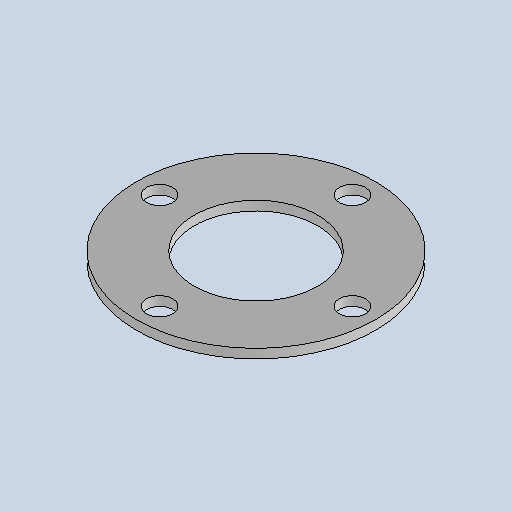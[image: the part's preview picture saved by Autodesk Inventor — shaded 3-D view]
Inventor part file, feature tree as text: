
AUTODESK INVENTOR PART (.ipt)
format: ipt  version: 2025.1 (Build 291241020, 241B)  size: 143,872 bytes
history: native  units: mm
features: other x3, sketch x2, sheet_metal_op x1, pattern_circular x1
ambient origin geometry x8: Origin, YZ Plane, XZ Plane, XY Plane, X Axis, Y Axis, Z Axis, Center Point
bodies: Solid1 (feature_tree)
feature tree (7):
  sheet_metal_op  "Face1"
  pattern_circular  "Circular Pattern1"  Count=8  [1 undecoded]
  sketch  "Sketch1"  dims[d2=6.0mm]
  other  "Plate1"
  sketch  "Sketch5"  dims[d22=155.0mm d23=80.0mm d24=62.5mm d25=17.0mm d26=6.0mm d27=0.0mm d28=40.0mm d29=360.0deg]
  other  "Cut1"
  other  "Definition1"
note: 1 required parameter value undecoded (feature->parameter linkage not recoverable at this tier; creation-order binding heuristic only, values carry confidence <= 0.55)
